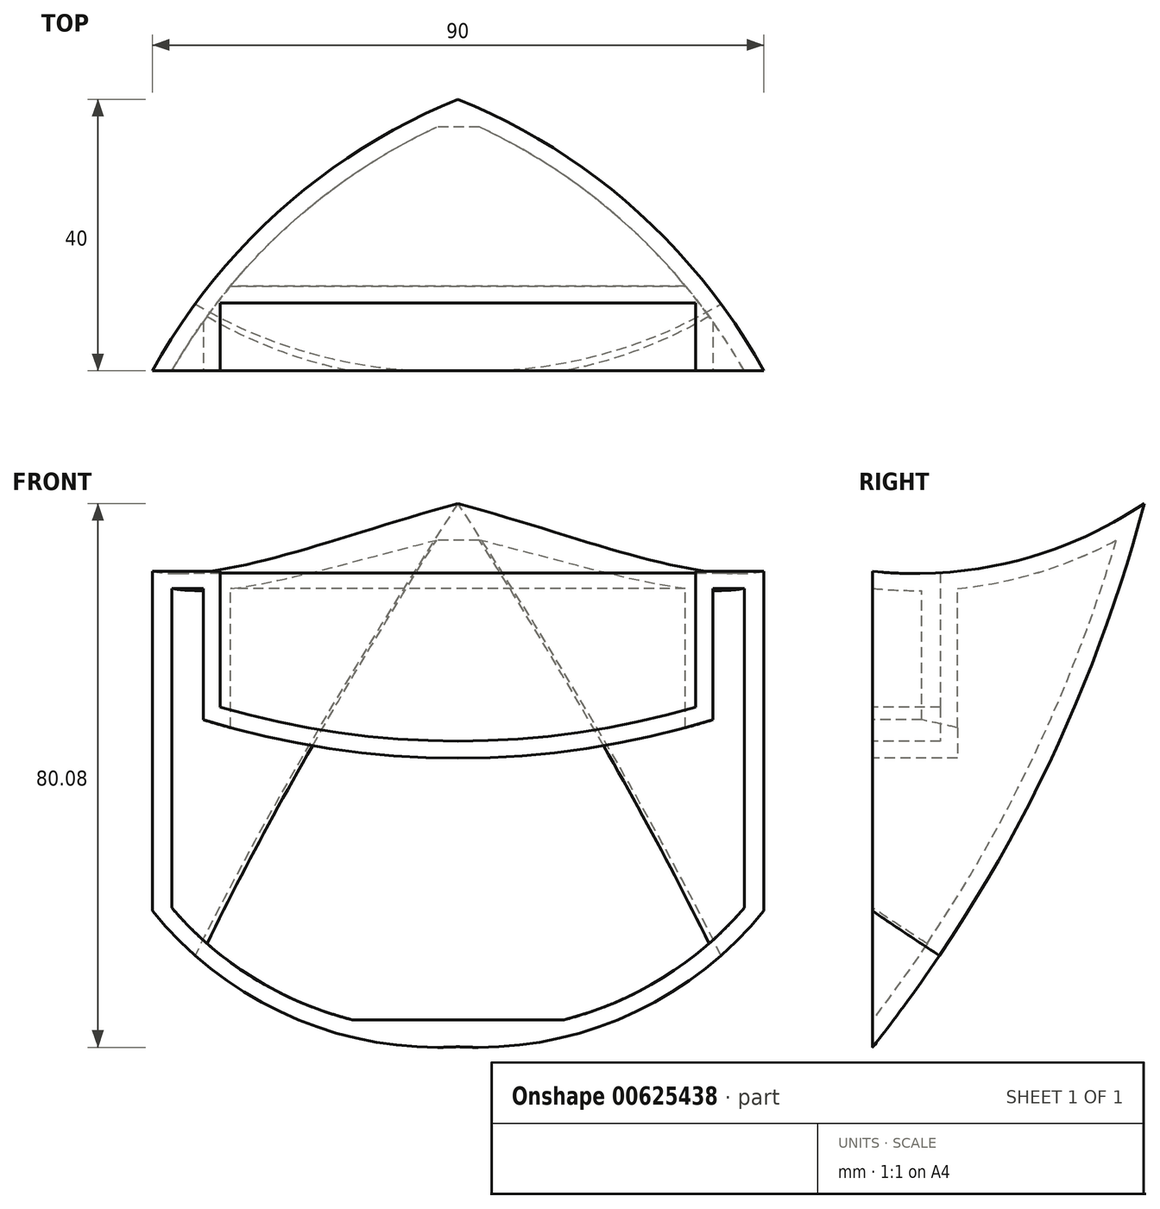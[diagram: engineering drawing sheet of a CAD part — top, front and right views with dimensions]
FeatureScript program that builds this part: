
annotation { "Feature Type Name" : "Feature", "Feature Type Description" : "" }
export const myFeature = defineFeature(function(context is Context, id is Id, definition is map)
    precondition{}
    {
        {
            var Q0;
            Q0=qCreatedBy(makeId("Front.planeOp"),FACE);
            var sketch = newSketch(context, id + "F0", { "sketchPlane" : qUnion([Q0])});
            skLineSegment(sketch, "E0.top", {"start": v(45, -25) * mm, "end": v(-45, -25) * mm});
            skLineSegment(sketch, "E0.left", {"start": v(45, 25) * mm, "end": v(45, -25) * mm});
            skLineSegment(sketch, "E0.right", {"start": v(-45, 25) * mm, "end": v(-45, -25) * mm});
            skPoint(sketch, "E0.middle", {"position": v(0, 0) * mm});
            skLineSegment(sketch, "E1", {"start": v(0, 0) * mm, "end": v(0, -45) * mm});
            skPoint(sketch, "E1.endSnap0", {"position": v(0, -25) * mm});
            skLineSegment(sketch, "E2", {"start": v(-45, 25) * mm, "end": v(-35, 25) * mm});
            skLineSegment(sketch, "E3", {"start": v(45, 25) * mm, "end": v(35, 25) * mm});
            skLineSegment(sketch, "E4", {"start": v(35, 25) * mm, "end": v(35, 5) * mm});
            skLineSegment(sketch, "E5", {"start": v(-35, 25) * mm, "end": v(-35, 5) * mm});
            skArc(sketch, "E6", {"start": v(-35, 5) * mm, "mid": v(0, 0) * mm, "end": v(35, 5) * mm});
            skArc(sketch, "E7", {"start": v(0, -45) * mm, "mid": v(24.91, -40.43) * mm, "end": v(45, -25) * mm});
            skArc(sketch, "E8", {"start": v(-45, -25) * mm, "mid": v(-24.91, -40.43) * mm, "end": v(0, -45) * mm});
            skLineSegment(sketch, "E9", {"start": v(45, 25) * mm, "end": v(45, 35) * mm});
            skLineSegment(sketch, "E10", {"start": v(-45, 25) * mm, "end": v(-45, 35) * mm});
            skArc(sketch, "E11", {"start": v(35, 25) * mm, "mid": v(42.07, 27.93) * mm, "end": v(45, 35) * mm});
            skArc(sketch, "E12", {"start": v(-45, 35) * mm, "mid": v(-42.07, 27.93) * mm, "end": v(-35, 25) * mm});
            skSolve(sketch);
        }
        {
            var Q0;
            Q0=qCreatedBy(makeId("Right.planeOp"),FACE);
            var sketch = newSketch(context, id + "F1", { "sketchPlane" : qUnion([Q0])});
            skArc(sketch, "E13", {"start": v(0, -45.08) * mm, "mid": v(24.13, -7.1) * mm, "end": v(40, 35) * mm});
            skArc(sketch, "E14", {"start": v(0, 25) * mm, "mid": v(20.89, 26.46) * mm, "end": v(40, 35) * mm});
            skLineSegment(sketch, "E15", {"start": v(0, 25) * mm, "end": v(0, -45.08) * mm});
            skSolve(sketch);
        }
        {
            var Q0;
            Q0=qCreatedBy(makeId("Top.planeOp"),FACE);
            var sketch = newSketch(context, id + "F2", { "sketchPlane" : qUnion([Q0])});
            skLineSegment(sketch, "E16.0", {"start": v(0, 0) * mm, "end": v(45, 0) * mm});
            skArc(sketch, "E17", {"start": v(0, 40) * mm, "mid": v(-25.94, 23.87) * mm, "end": v(-45, 0) * mm});
            skArc(sketch, "E18", {"start": v(45, 0) * mm, "mid": v(25.94, 23.87) * mm, "end": v(0, 40) * mm});
            skLineSegment(sketch, "E19", {"start": v(-45, 0) * mm, "end": v(-45, 75.49) * mm});
            skLineSegment(sketch, "E20", {"start": v(-45, 75.49) * mm, "end": v(49.67, 75.49) * mm});
            skLineSegment(sketch, "E21", {"start": v(49.67, 75.49) * mm, "end": v(45, 0) * mm});
            skLineSegment(sketch, "E22", {"start": v(-45, 75.49) * mm, "end": v(-45, 0) * mm});
            skSolve(sketch);
        }
        {
            var Q0;
            Q0 = qSketchRegion(id + "F1", true);
            extrude(context, id + "F3", {"entities" : qUnion([Q0]), "depth" : 45 * mm, "offsetDistance" : 25 * mm});
        }
        {
            var Q0;
            Q0 = qSketchRegion(id + "F1", true);
            extrude(context, id + "F4", {"entities" : qUnion([Q0]), "operationType" : NewBodyOperationType.ADD, "depth" : -45 * mm, "offsetDistance" : 25 * mm});
        }
        {
            var Q0;
            Q0 = qSketchRegion(id + "F2", true);
            extrude(context, id + "F5", {"entities" : qUnion([Q0]), "operationType" : NewBodyOperationType.REMOVE, "oppositeDirection" : true, "depth" : 45 * mm, "offsetDistance" : 25 * mm});
        }
        {
            var Q0;
            Q0 = qSketchRegion(id + "F2", true);
            extrude(context, id + "F6", {"entities" : qUnion([Q0]), "operationType" : NewBodyOperationType.REMOVE, "oppositeDirection" : true, "depth" : -45 * mm, "offsetDistance" : 25 * mm});
        }
        {
            var Q0;
            Q0=qCreatedBy(makeId("Front.planeOp"),FACE);
            var sketch = newSketch(context, id + "F7", { "sketchPlane" : qUnion([Q0])});
            skArc(sketch, "E23.0", {"start": v(0, -45) * mm, "mid": v(24.91, -40.43) * mm, "end": v(45, -25) * mm});
            skArc(sketch, "E24.0", {"start": v(-45, -25) * mm, "mid": v(-24.91, -40.43) * mm, "end": v(0, -45) * mm});
            skLineSegment(sketch, "E25", {"start": v(-45, -25) * mm, "end": v(-109.21, -26.83) * mm});
            skLineSegment(sketch, "E26", {"start": v(-109.21, -26.83) * mm, "end": v(-21.9, -71.57) * mm});
            skLineSegment(sketch, "E27", {"start": v(-21.9, -71.57) * mm, "end": v(71.6, -68.14) * mm});
            skLineSegment(sketch, "E28", {"start": v(71.6, -68.14) * mm, "end": v(45, -25) * mm});
            skSolve(sketch);
        }
        {
            var Q0;
            Q0 = qSketchRegion(id + "F7", true);
            extrude(context, id + "F8", {"entities" : qUnion([Q0]), "operationType" : NewBodyOperationType.REMOVE, "oppositeDirection" : true, "depth" : 25 * mm, "offsetDistance" : 25 * mm});
        }
        {
            var Q0;
            Q0=qCreatedBy(makeId("Front.planeOp"),FACE);
            var sketch = newSketch(context, id + "F9", { "sketchPlane" : qUnion([Q0])});
            skLineSegment(sketch, "E29.0", {"start": v(-35, 25) * mm, "end": v(-35, 5) * mm});
            skArc(sketch, "E30.0", {"start": v(-35, 5) * mm, "mid": v(0, 0) * mm, "end": v(35, 5) * mm});
            skLineSegment(sketch, "E31.0", {"start": v(35, 25) * mm, "end": v(35, 5) * mm});
            skLineSegment(sketch, "E32", {"start": v(35, 25) * mm, "end": v(-35, 25) * mm});
            skSolve(sketch);
        }
        {
            var Q0;
            Q0 = qSketchRegion(id + "F9", true);
            extrude(context, id + "F10", {"entities" : qUnion([Q0]), "operationType" : NewBodyOperationType.REMOVE, "oppositeDirection" : true, "depth" : 10 * mm, "offsetDistance" : 25 * mm});
        }
        {
            var Q0;
            {var subQ0=sQuery(id+"F1.wireOp",EDGE,"E15");Q0=makeQuery(id+"F4.boolean.opBoolean","MERGE",FACE,{"derivedFrom":[makeQuery(id+"F3.opExtrude","SWEPT_FACE",FACE,{"disambiguationData":[OSD([subQ0])]}),makeQuery(id+"F4.opExtrude","SWEPT_FACE",FACE,{"disambiguationData":[OSD([subQ0])]})]});}
            shell(context, id + "F11", {"entities" : qUnion([Q0]), "thickness" : 2.5 * mm});
        }
    });
